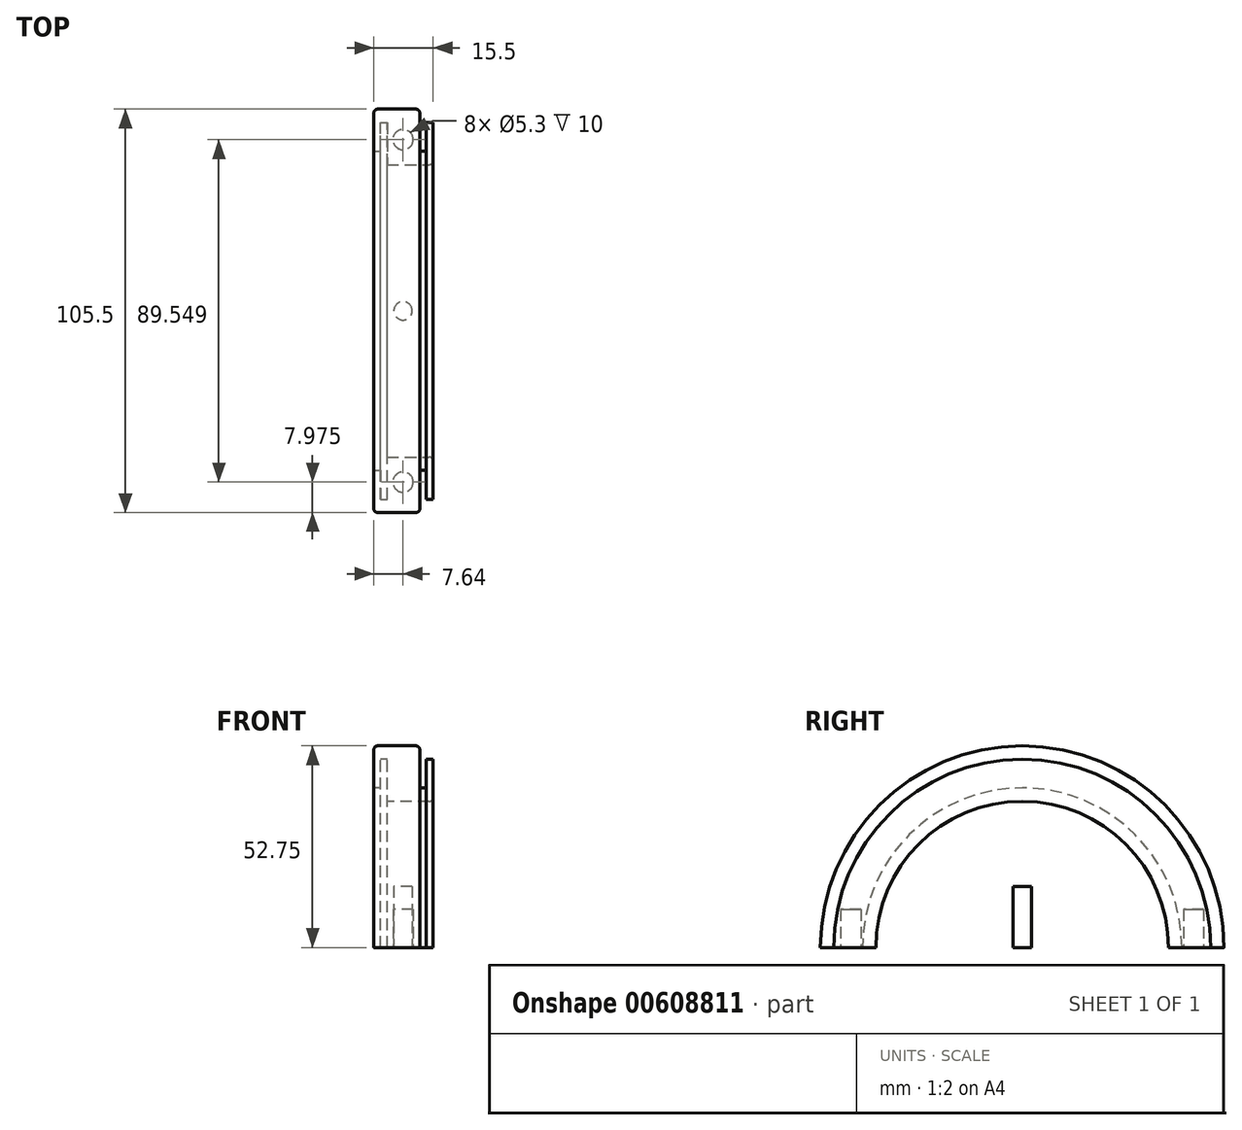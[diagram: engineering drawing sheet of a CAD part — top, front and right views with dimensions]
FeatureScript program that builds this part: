
annotation { "Feature Type Name" : "Feature", "Feature Type Description" : "" }
export const myFeature = defineFeature(function(context is Context, id is Id, definition is map)
    precondition{}
    {
        {
            var Q0;
            Q0=qCreatedBy(makeId("Top.planeOp"),FACE);
            var sketch = newSketch(context, id + "F0", { "sketchPlane" : qUnion([Q0])});
            skLineSegment(sketch, "E0.bottom", {"start": v(-7.64, 41.75) * mm, "end": v(-5.84, 41.75) * mm});
            skLineSegment(sketch, "E0.left", {"start": v(-7.64, 41.75) * mm, "end": v(-7.64, 52.75) * mm});
            skLineSegment(sketch, "E0.right", {"start": v(-5.84, 41.75) * mm, "end": v(-5.84, 49.25) * mm});
            skLineSegment(sketch, "E1.bottom", {"start": v(-7.64, 52.75) * mm, "end": v(4.36, 52.75) * mm});
            skLineSegment(sketch, "E1.top", {"start": v(-5.84, 49.25) * mm, "end": v(-4.14, 49.25) * mm});
            skLineSegment(sketch, "E2.left", {"start": v(4.36, 52.75) * mm, "end": v(4.36, 41.75) * mm});
            skLineSegment(sketch, "E2.right", {"start": v(-4.14, 49.25) * mm, "end": v(-4.14, 38.25) * mm});
            skLineSegment(sketch, "E3.bottom", {"start": v(-4.14, 38.25) * mm, "end": v(7.86, 38.25) * mm});
            skLineSegment(sketch, "E3.top", {"start": v(4.36, 41.75) * mm, "end": v(6.06, 41.75) * mm});
            skLineSegment(sketch, "E4.top", {"start": v(7.86, 49.25) * mm, "end": v(6.06, 49.25) * mm});
            skLineSegment(sketch, "E4.left", {"start": v(7.86, 38.25) * mm, "end": v(7.86, 49.25) * mm});
            skLineSegment(sketch, "E4.right", {"start": v(6.06, 41.75) * mm, "end": v(6.06, 49.25) * mm});
            skLineSegment(sketch, "E5", {"start": v(-17.77, 0) * mm, "end": v(0, 0) * mm});
            skLineSegment(sketch, "E6", {"start": v(-4.14, 49.25) * mm, "end": v(-4.14, 0) * mm});
            skSolve(sketch);
        }
        {
            var Q0;
            Q0 = qSketchRegion(id + "F0", true);
            var Q1;
            Q1=sQuery(id+"F0.wireOp",EDGE,"E5");
            revolve(context, id + "F1", {"entities" : qUnion([Q0]), "axis" : qUnion([Q1]), "revolveType" : RevolveType.ONE_DIRECTION, "angle" : 180 * degree});
        }
        {
            var Q0;
            Q0=qCreatedBy(makeId("Top.planeOp"),FACE);
            var sketch = newSketch(context, id + "F2", { "sketchPlane" : qUnion([Q0])});
            skCircle(sketch, "E7", {"center": v(0, 44.77) * mm, "radius": 2.65 * mm});
            skCircle(sketch, "E8.MirrorC", {"center": v(0, -44.77) * mm, "radius": 2.65 * mm});
            skSolve(sketch);
        }
        {
            var Q0;
            Q0 = qSketchRegion(id + "F2", true);
            var Q1;
            Q1 = qSketchRegion(id + "F4", true);
            extrude(context, id + "F3", {"entities" : qUnion([Q0, Q1]), "operationType" : NewBodyOperationType.REMOVE, "depth" : 10 * mm, "offsetDistance" : 25 * mm});
        }
        {
            var Q0;
            Q0=qCreatedBy(makeId("Top.planeOp"),FACE);
            var sketch = newSketch(context, id + "F4", { "sketchPlane" : qUnion([Q0])});
            skCircle(sketch, "E9.MirrorC", {"center": v(-0.02, 0) * mm, "radius": 2.4 * mm});
            skSolve(sketch);
        }
        {
            var Q0;
            Q0 = qSketchRegion(id + "F4", true);
            extrude(context, id + "F5", {"entities" : qUnion([Q0]), "depth" : 16 * mm, "offsetDistance" : 25 * mm});
        }
        {
            var Q0;
            Q0=makeQuery(id+"F1.opRevolve","SWEPT_EDGE",EDGE,{"disambiguationData":[OSD([sQuery(id+"F0.wireOp",EDGE,"E3.bottom"),sQuery(id+"F0.wireOp",EDGE,"E4.left")])]});
            var Q1;
            Q1=makeQuery(id+"F1.opRevolve","SWEPT_EDGE",EDGE,{"disambiguationData":[OSD([sQuery(id+"F0.wireOp",EDGE,"E1.bottom"),sQuery(id+"F0.wireOp",EDGE,"E2.left")])]});
            var Q2;
            Q2=makeQuery(id+"F1.opRevolve","SWEPT_EDGE",EDGE,{"disambiguationData":[OSD([sQuery(id+"F0.wireOp",EDGE,"E0.left"),sQuery(id+"F0.wireOp",EDGE,"E1.bottom")])]});
            fillet(context, id + "F6", {"entities" : qUnion([Q0, Q1, Q2]), "radius" : 1 * mm, "tangentPropagation" : true, "allowEdgeOverflow" : false});
        }
    });
